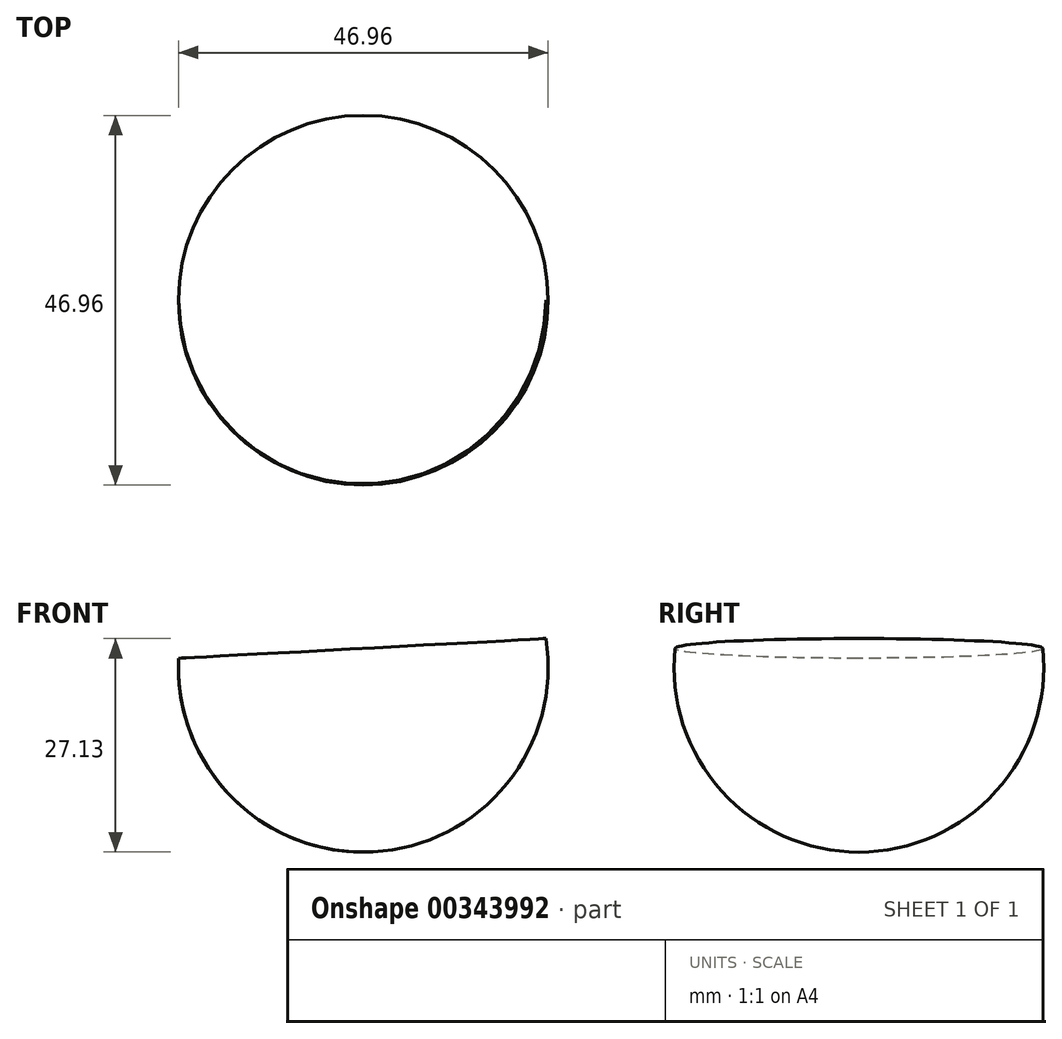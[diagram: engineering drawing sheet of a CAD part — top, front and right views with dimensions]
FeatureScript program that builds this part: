
annotation { "Feature Type Name" : "Feature", "Feature Type Description" : "" }
export const myFeature = defineFeature(function(context is Context, id is Id, definition is map)
    precondition{}
    {
        {
            var Q0;
            Q0=qCreatedBy(makeId("Front.planeOp"),FACE);
            var sketch = newSketch(context, id + "F0", { "sketchPlane" : qUnion([Q0])});
            skArc(sketch, "E0", {"start": v(-24.71, 24.59) * mm, "mid": v(-17.82, 6.8) * mm, "end": v(0, 0) * mm});
            skLineSegment(sketch, "E1", {"start": v(0, 0) * mm, "end": v(-1.26, 23.45) * mm});
            skSolve(sketch);
        }
        {
            var Q0;
            Q0=sQuery(id+"F0.wireOp",EDGE,"E0");
            var Q1;
            Q1=sQuery(id+"F0.wireOp",EDGE,"E1");
            revolve(context, id + "F1", {"bodyType" : ToolBodyType.SURFACE, "surfaceEntities" : qUnion([Q0]), "axis" : qUnion([Q1]), "revolveType" : RevolveType.FULL});
        }
    });
